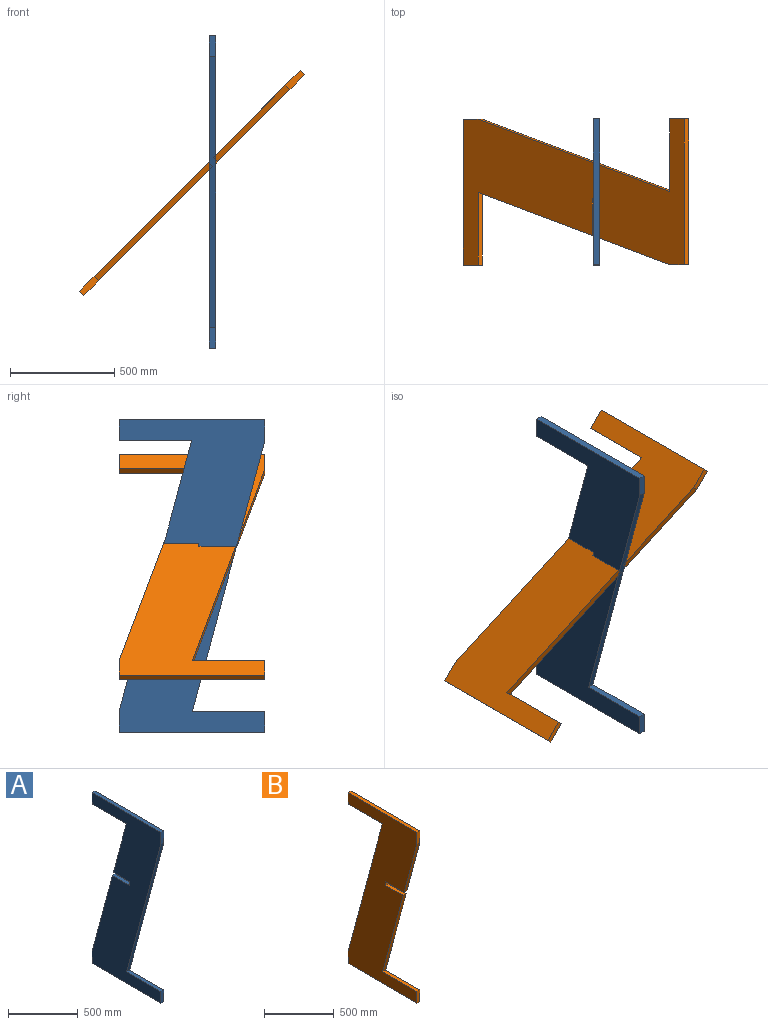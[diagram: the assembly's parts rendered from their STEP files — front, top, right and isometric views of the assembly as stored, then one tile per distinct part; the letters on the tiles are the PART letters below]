
ASSEMBLY  parts=2 mates=1
PART A: 16 faces, bbox 30x700x1500 mm
  f0: plane 492x131.83mm, normal (0,0.97,0.26), area 15280.7mm2, adj f1,f2,f8,f13
  f1: plane 1500x700mm, normal (1,0,0), area 591509.3mm2, adj f0,f3,f4,f5,f6,f7,f8,f9
  f2: plane 1500x700mm, normal (-1,0,0), area 591509.3mm2, adj f0,f3,f4,f5,f6,f7,f8,f9
  f3: plane 348.33x30mm, normal (0,0,1), area 10450mm2, adj f1,f2,f4,f12
  f4: plane 100x30mm, normal (0,-1,0), area 3000mm2, adj f1,f2,f3,f5
  f5: plane 700x30mm, normal (0,0,-1), area 21000mm2, adj f1,f2,f4,f6
  f6: plane 100x30mm, normal (0,1,0), area 3000mm2, adj f1,f2,f5,f7
  f7: plane 775x207.66mm, normal (0,0.97,0.26), area 24070.2mm2, adj f1,f2,f6,f15
  f8: plane 348.33x30mm, normal (0,0,-1), area 10450mm2, adj f0,f1,f2,f9
  f9: plane 100x30mm, normal (0,1,0), area 3000mm2, adj f1,f2,f8,f10
  f10: plane 700x30mm, normal (0,0,1), area 21000mm2, adj f1,f2,f9,f11
  f11: plane 100x30mm, normal (0,-1,0), area 3000mm2, adj f1,f2,f10,f12
  f12: plane 1300x348.33mm, normal (0,-0.97,-0.26), area 40375.8mm2, adj f1,f2,f3,f11
  f13: plane 166.99x30mm, normal (0,0,-1), area 5009.7mm2, adj f0,f1,f2,f14
  f14: plane 33x30mm, normal (0,1,0), area 990mm2, adj f1,f2,f13,f15
  f15: plane 175.83x30mm, normal (0,0,1), area 5275mm2, adj f1,f2,f7,f14
PART B: 16 faces, bbox 30x700x1500 mm
  f0: plane 775x207.66mm, normal (0,-0.97,-0.26), area 24070.2mm2, adj f1,f11,f12,f15
  f1: plane 348.33x30mm, normal (0,0,1), area 10450mm2, adj f0,f2,f11,f12
  f2: plane 100x30mm, normal (0,-1,0), area 3000mm2, adj f1,f3,f11,f12
  f3: plane 700x30mm, normal (0,0,-1), area 21000mm2, adj f2,f4,f11,f12
  f4: plane 100x30mm, normal (0,1,0), area 3000mm2, adj f3,f5,f11,f12
  f5: plane 1300x348.33mm, normal (0,0.97,0.26), area 40375.8mm2, adj f4,f6,f11,f12
  f6: plane 348.33x30mm, normal (0,0,-1), area 10450mm2, adj f5,f7,f11,f12
  f7: plane 100x30mm, normal (0,1,0), area 3000mm2, adj f6,f8,f11,f12
  f8: plane 700x30mm, normal (0,0,1), area 21000mm2, adj f7,f9,f11,f12
  f9: plane 100x30mm, normal (0,-1,0), area 3000mm2, adj f8,f10,f11,f12
  f10: plane 492x131.83mm, normal (0,-0.97,-0.26), area 15280.7mm2, adj f9,f11,f12,f14
  f11: plane 1500x700mm, normal (1,0,0), area 591217.5mm2, adj f0,f1,f2,f3,f4,f5,f6,f7
  f12: plane 1500x700mm, normal (-1,0,0), area 591217.5mm2, adj f0,f1,f2,f3,f4,f5,f6,f7
  f13: plane 33x30mm, normal (0,-1,0), area 990mm2, adj f11,f12,f14,f15
  f14: plane 184.68x30mm, normal (0,0,-1), area 5540.3mm2, adj f10,f11,f12,f13
  f15: plane 175.83x30mm, normal (0,0,1), area 5275mm2, adj f0,f11,f12,f13
PLACE A t=(76.71,556.7,-353.23)mm
PLACE B rot(axis=(0,1,0),45deg) t=(-547.16,556.7,-79.29)mm
MATE planar B.f13 <-> A.f14  axis (0,-1,0) through (93.83,173.2,540.48)mm
